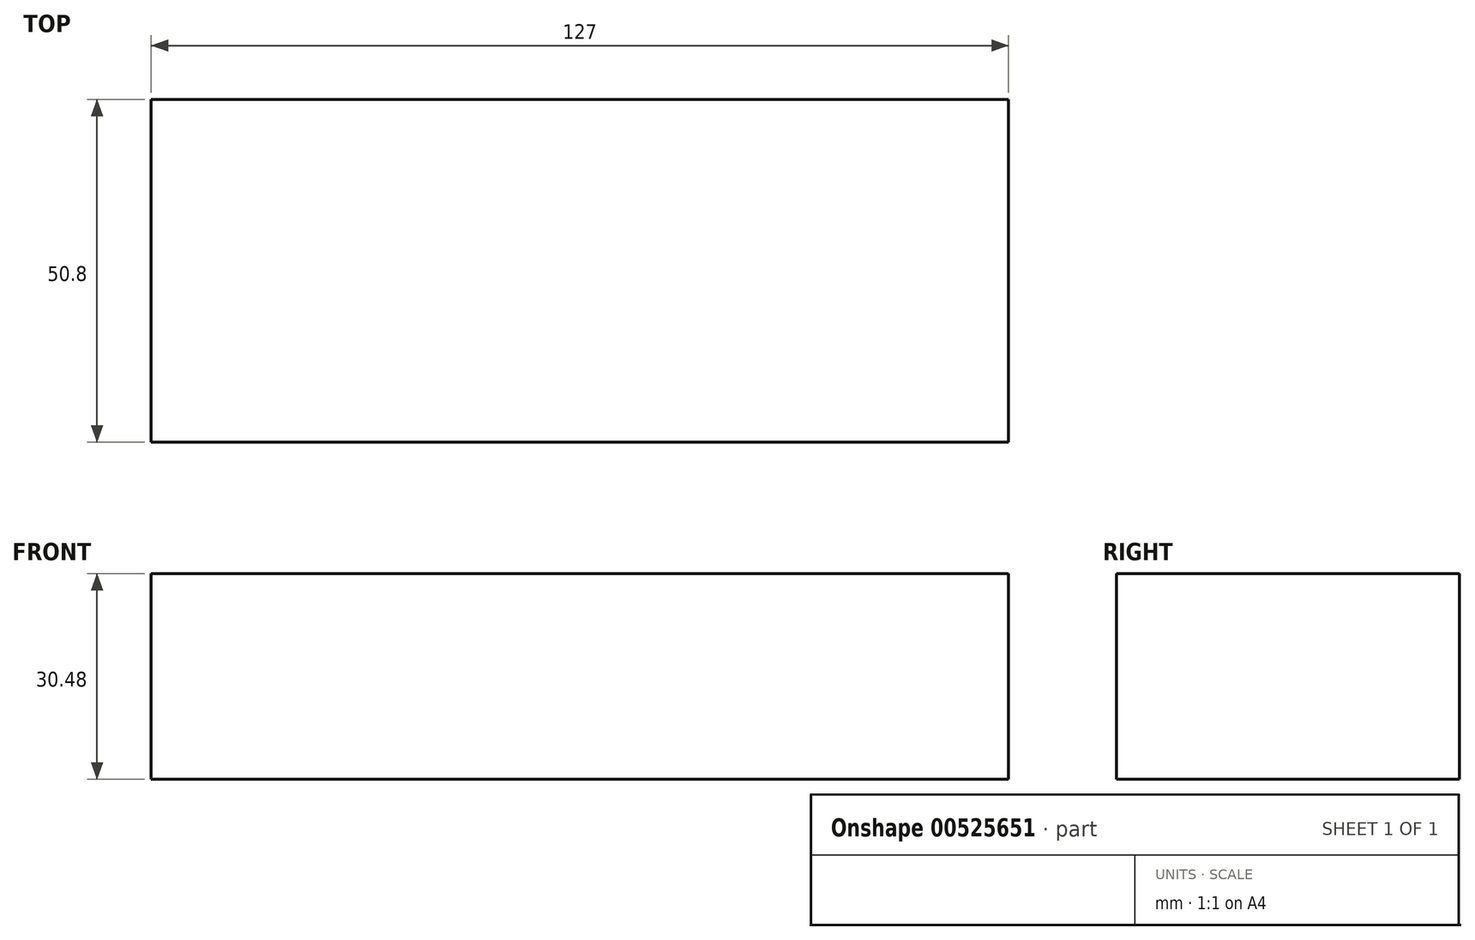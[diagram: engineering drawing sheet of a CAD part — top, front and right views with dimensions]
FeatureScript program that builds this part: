
annotation { "Feature Type Name" : "Feature", "Feature Type Description" : "" }
export const myFeature = defineFeature(function(context is Context, id is Id, definition is map)
    precondition{}
    {
        {
            var Q0;
            Q0=qCreatedBy(makeId("Top.planeOp"),FACE);
            var sketch = newSketch(context, id + "F0", { "sketchPlane" : qUnion([Q0])});
            skLineSegment(sketch, "E0.bottom", {"start": v(0, 0) * mm, "end": v(127, 0) * mm});
            skLineSegment(sketch, "E0.top", {"start": v(0, 50.8) * mm, "end": v(127, 50.8) * mm});
            skLineSegment(sketch, "E0.left", {"start": v(0, 0) * mm, "end": v(0, 50.8) * mm});
            skLineSegment(sketch, "E0.right", {"start": v(127, 0) * mm, "end": v(127, 50.8) * mm});
            skSolve(sketch);
        }
        {
            var Q0;
            Q0=makeQuery(id+"F0.imprint","IMPRINT",FACE,{"disambiguationData":[TD([[makeQuery(id+"F0.imprint","IMPRINT",EDGE,{"derivedFrom":sQuery(id+"F0.wireOp",EDGE,"E0.bottom")}),1.0]])]});
            extrude(context, id + "F1", {"entities" : qUnion([Q0]), "depth" : 30.48 * mm, "offsetDistance" : 25.4 * mm});
        }
    });
